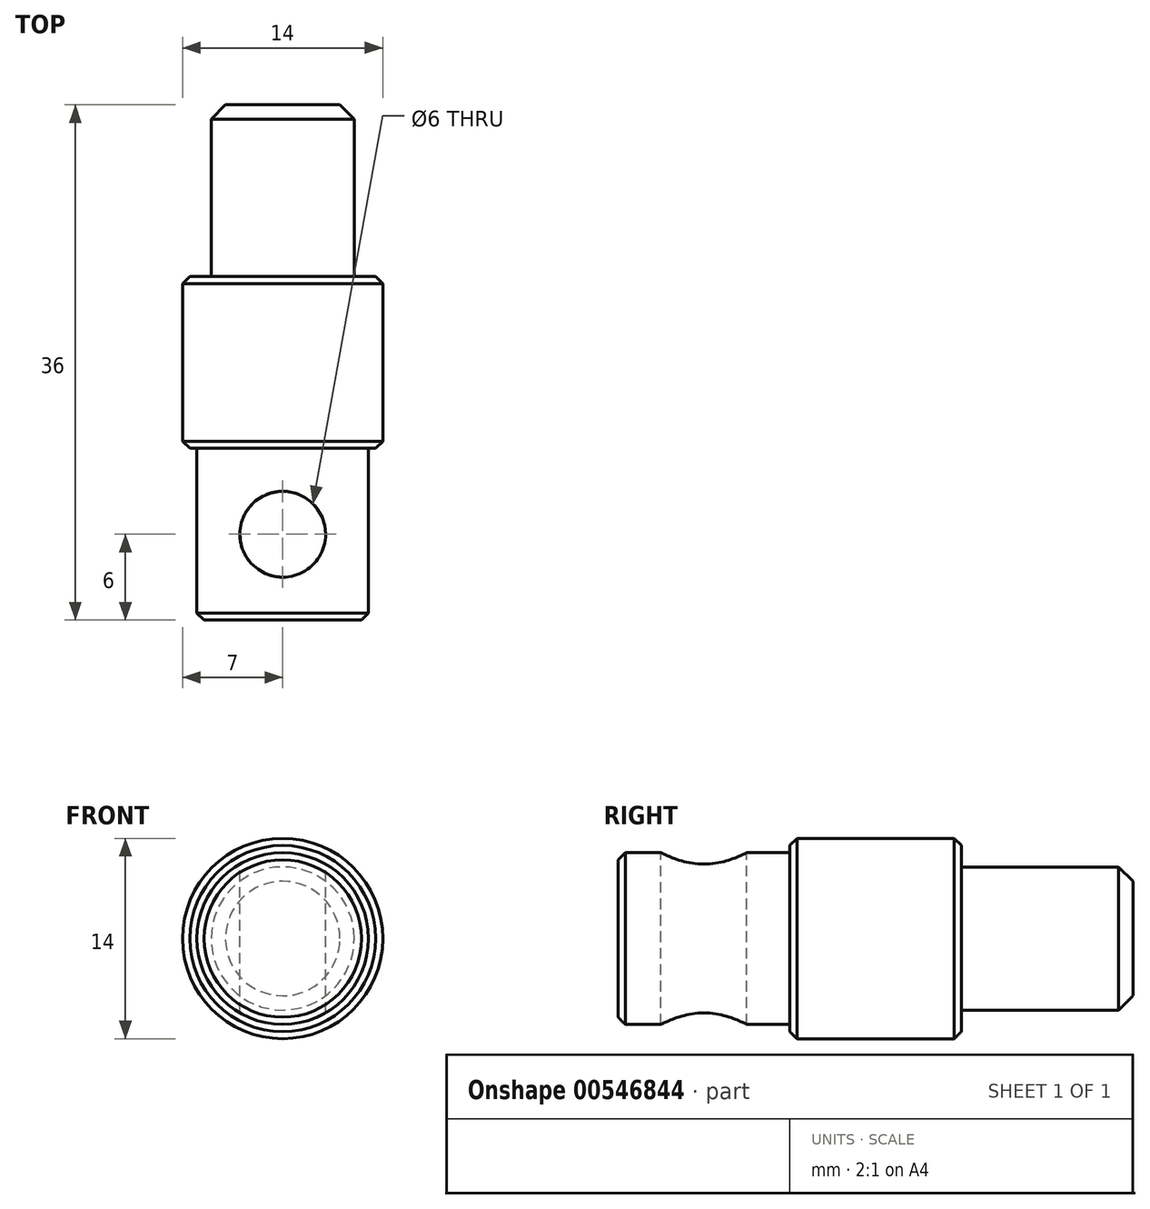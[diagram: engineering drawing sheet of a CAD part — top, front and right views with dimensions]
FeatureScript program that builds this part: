
annotation { "Feature Type Name" : "Feature", "Feature Type Description" : "" }
export const myFeature = defineFeature(function(context is Context, id is Id, definition is map)
    precondition{}
    {
        {
            var Q0;
            Q0=qCreatedBy(makeId("Front.planeOp"),FACE);
            var sketch = newSketch(context, id + "F0", { "sketchPlane" : qUnion([Q0])});
            skCircle(sketch, "E0", {"center": v(0, 0) * mm, "radius": 6 * mm});
            skCircle(sketch, "E1", {"center": v(0, 0) * mm, "radius": 5 * mm});
            skCircle(sketch, "E2", {"center": v(0, 0) * mm, "radius": 7 * mm});
            skSolve(sketch);
        }
        {
            var Q0;
            Q0=makeQuery(id+"F0.imprint","IMPRINT",FACE,{"disambiguationData":[TD([[makeQuery(id+"F0.imprint","IMPRINT",EDGE,{"derivedFrom":sQuery(id+"F0.wireOp",EDGE,"E0")}),-1.0]])]});
            extrude(context, id + "F1", {"entities" : qUnion([Q0]), "depth" : 12 * mm, "offsetDistance" : 25 * mm});
        }
        {
            var Q0;
            Q0=makeQuery(id+"F0.imprint","IMPRINT",FACE,{"disambiguationData":[TD([[makeQuery(id+"F0.imprint","IMPRINT",EDGE,{"derivedFrom":sQuery(id+"F0.wireOp",EDGE,"E0")}),1.0]])]});
            extrude(context, id + "F2", {"entities" : qUnion([Q0]), "operationType" : NewBodyOperationType.ADD, "depth" : 24 * mm, "offsetDistance" : 25 * mm});
        }
        {
            var Q0;
            Q0=makeQuery(id+"F0.imprint","IMPRINT",FACE,{"disambiguationData":[TD([[makeQuery(id+"F0.imprint","IMPRINT",EDGE,{"derivedFrom":sQuery(id+"F0.wireOp",EDGE,"E1")}),1.0]])]});
            extrude(context, id + "F3", {"entities" : qUnion([Q0]), "operationType" : NewBodyOperationType.ADD, "depth" : 24 * mm, "offsetDistance" : 25 * mm, "hasSecondDirection" : true, "secondDirectionOppositeDirection" : true, "secondDirectionDepth" : 12 * mm});
        }
        {
            var Q0;
            Q0=makeQuery(id+"F3.opExtrude","CAP_EDGE",EDGE,{"disambiguationData":[OSD([sQuery(id+"F0.wireOp",EDGE,"E1")])],"isStart":true});
            chamfer(context, id + "F4", {"entities" : qUnion([Q0]), "width" : 1 * mm, "tangentPropagation" : true});
        }
        {
            var Q0;
            Q0=makeQuery(id+"F2.opExtrude","CAP_EDGE",EDGE,{"disambiguationData":[OSD([sQuery(id+"F0.wireOp",EDGE,"E0")])],"isStart":false});
            var Q1;
            Q1=makeQuery(id+"F1.opExtrude","CAP_EDGE",EDGE,{"disambiguationData":[OSD([sQuery(id+"F0.wireOp",EDGE,"E2")])],"isStart":false});
            var Q2;
            Q2=makeQuery(id+"F1.opExtrude","SWEPT_FACE",FACE,{"disambiguationData":[OSD([sQuery(id+"F0.wireOp",EDGE,"E2")])]});
            chamfer(context, id + "F5", {"entities" : qUnion([Q0, Q1, Q2]), "width" : .5 * mm, "tangentPropagation" : true});
        }
        {
            var Q0;
            Q0=qCreatedBy(makeId("Top.planeOp"),FACE);
            var sketch = newSketch(context, id + "F6", { "sketchPlane" : qUnion([Q0])});
            skLineSegment(sketch, "E3", {"start": v(0, 0) * mm, "end": v(0, -18) * mm, "construction": true});
            skLineSegment(sketch, "E4", {"start": v(0, -18) * mm, "end": v(25, -18) * mm, "construction": true});
            skCircle(sketch, "E5", {"center": v(0, -18) * mm, "radius": 3 * mm});
            skSolve(sketch);
        }
        {
            var Q0;
            Q0 = qSketchRegion(id + "F6", true);
            extrude(context, id + "F7", {"entities" : qUnion([Q0]), "operationType" : NewBodyOperationType.REMOVE, "oppositeDirection" : true, "depth" : 25 * mm, "offsetDistance" : 25 * mm, "hasSecondDirection" : true, "secondDirectionOppositeDirection" : false, "secondDirectionDepth" : 25 * mm});
        }
    });
